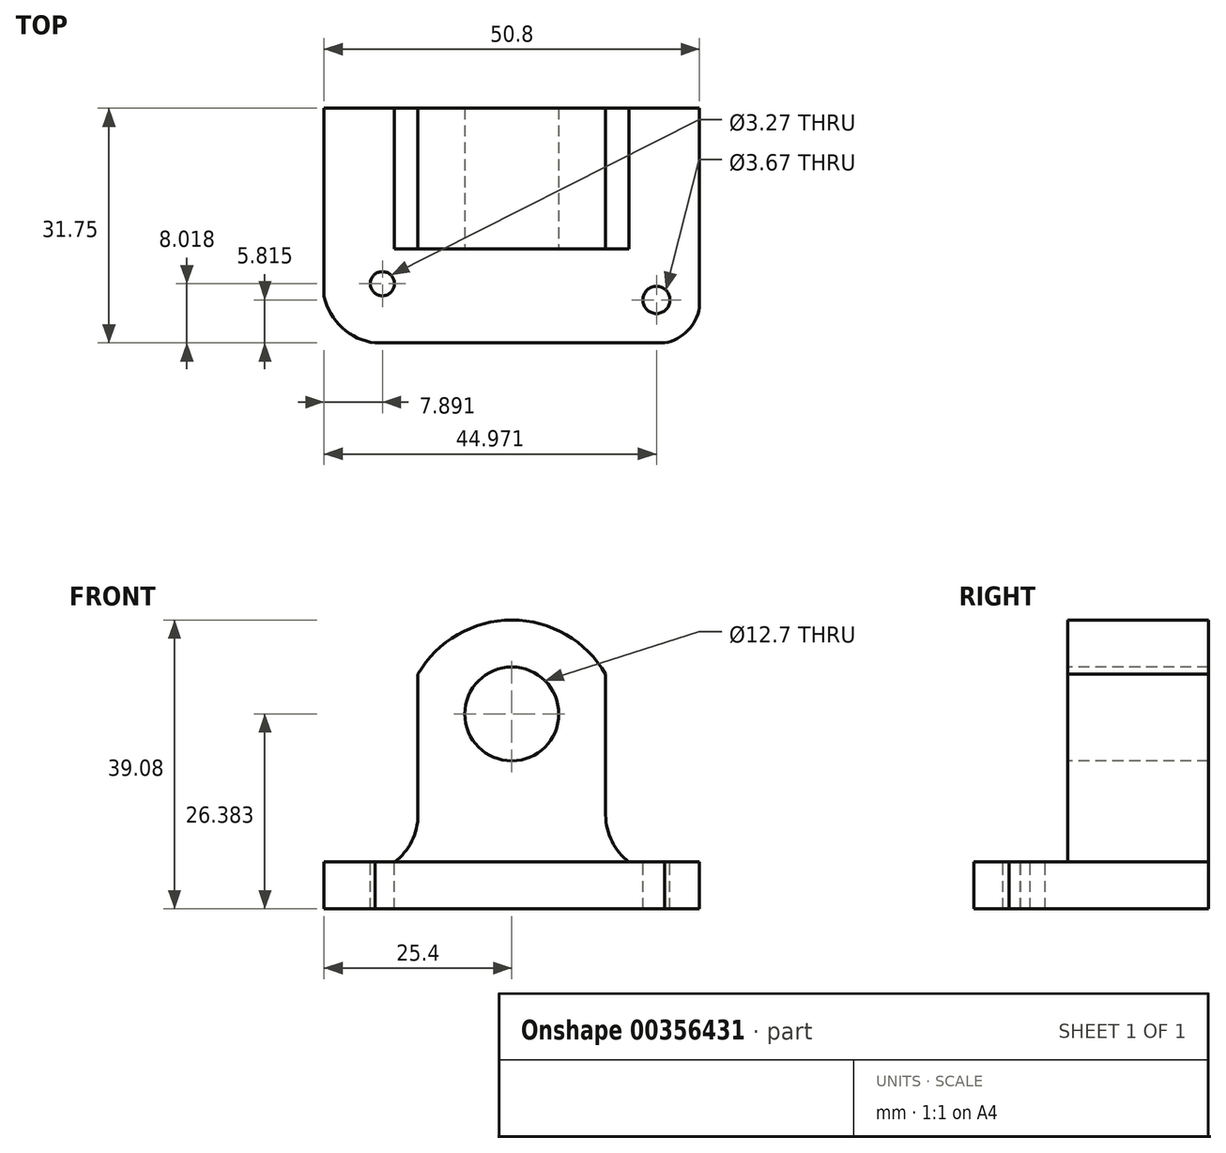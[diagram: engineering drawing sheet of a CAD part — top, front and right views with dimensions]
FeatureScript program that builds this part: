
annotation { "Feature Type Name" : "Feature", "Feature Type Description" : "" }
export const myFeature = defineFeature(function(context is Context, id is Id, definition is map)
    precondition{}
    {
        {
            var Q0;
            Q0=qCreatedBy(makeId("Front.planeOp"),FACE);
            var sketch = newSketch(context, id + "F0", { "sketchPlane" : qUnion([Q0])});
            skLineSegment(sketch, "E0", {"start": v(0, 44.45) * mm, "end": v(0, 0) * mm});
            skLineSegment(sketch, "E1", {"start": v(0, 0) * mm, "end": v(50.8, 0) * mm});
            skLineSegment(sketch, "E2", {"start": v(50.8, 0) * mm, "end": v(50.8, 44.45) * mm});
            skLineSegment(sketch, "E3", {"start": v(50.8, 44.45) * mm, "end": v(0, 44.45) * mm});
            skSolve(sketch);
        }
        {
            var Q0;
            Q0 = qSketchRegion(id + "F0", true);
            extrude(context, id + "F1", {"entities" : qUnion([Q0]), "depth" : 31.75 * mm});
        }
        {
            var Q0;
            Q0=makeQuery(id+"F1.opExtrude","SWEPT_FACE",FACE,{"disambiguationData":[OSD([sQuery(id+"F0.wireOp",EDGE,"E3")])]});
            var sketch = newSketch(context, id + "F2", { "sketchPlane" : qUnion([Q0])});
            skLineSegment(sketch, "E4", {"start": v(0, -19.05) * mm, "end": v(50.8, -19.05) * mm});
            skSolve(sketch);
        }
        {
            var Q0;
            {var subQ0=sQuery(id+"F2.wireOp",EDGE,"E4");Q0=makeQuery(id+"F2.imprint","IMPRINT",FACE,{"disambiguationData":[TD([[makeQuery(id+"F2.imprint","IMPRINT",EDGE,{"derivedFrom":subQ0}),-1.0]])]});}
            extrude(context, id + "F3", {"entities" : qUnion([Q0]), "operationType" : NewBodyOperationType.REMOVE, "oppositeDirection" : true, "depth" : 38.1 * mm});
        }
        {
            var Q0;
            Q0=makeQuery(id+"F3.boolean.opBoolean","COPY",FACE,{"derivedFrom":makeQuery(id+"F3.opExtrude","SWEPT_FACE",FACE,{"disambiguationData":[OSD([sQuery(id+"F2.wireOp",EDGE,"E4")])]})});
            var sketch = newSketch(context, id + "F4", { "sketchPlane" : qUnion([Q0])});
            skLineSegment(sketch, "E5", {"start": v(38.1, 44.45) * mm, "end": v(38.1, 12.7) * mm});
            skArc(sketch, "E6", {"start": v(38.1, 12.7) * mm, "mid": v(42.49, 5.6) * mm, "end": v(50.8, 6.35) * mm});
            skLineSegment(sketch, "E7", {"start": v(12.7, 44.45) * mm, "end": v(12.7, 12.7) * mm});
            skArc(sketch, "E8", {"start": v(0, 6.35) * mm, "mid": v(8.31, 5.6) * mm, "end": v(12.7, 12.7) * mm});
            skSolve(sketch);
        }
        {
            var Q0;
            Q0 = qSketchRegion(id + "F4", true);
            var Q1;
            {var subQ3=sQuery(id+"F4.wireOp",EDGE,"E7");Q1=makeQuery(id+"F4.imprint","IMPRINT",FACE,{"disambiguationData":[TD([[makeQuery(id+"F4.imprint","IMPRINT",EDGE,{"derivedFrom":subQ3}),-1.0]])]});}
            var Q2;
            {var subQ3=sQuery(id+"F4.wireOp",EDGE,"E5");Q2=makeQuery(id+"F4.imprint","IMPRINT",FACE,{"disambiguationData":[TD([[makeQuery(id+"F4.imprint","IMPRINT",EDGE,{"derivedFrom":subQ3}),1.0]])]});}
            extrude(context, id + "F5", {"entities" : qUnion([Q0, Q1, Q2]), "operationType" : NewBodyOperationType.REMOVE, "oppositeDirection" : true, "depth" : 25.4 * mm});
        }
        {
            var Q0;
            Q0=makeQuery(id+"F3.boolean.opBoolean","COPY",FACE,{"derivedFrom":makeQuery(id+"F3.opExtrude","SWEPT_FACE",FACE,{"disambiguationData":[OSD([sQuery(id+"F2.wireOp",EDGE,"E4")])]})});
            var sketch = newSketch(context, id + "F6", { "sketchPlane" : qUnion([Q0])});
            skArc(sketch, "E9", {"start": v(38.1, 31.75) * mm, "mid": v(25.4, 39.08) * mm, "end": v(12.7, 31.75) * mm});
            skSolve(sketch);
        }
        {
            var Q0;
            Q0 = qSketchRegion(id + "F6", true);
            var Q1;
            {var subQ0=sQuery(id+"F6.wireOp",EDGE,"E9");Q1=makeQuery(id+"F6.imprint","IMPRINT",FACE,{"disambiguationData":[TD([[makeQuery(id+"F6.imprint","IMPRINT",EDGE,{"derivedFrom":subQ0}),-1.0]])]});}
            extrude(context, id + "F7", {"entities" : qUnion([Q0, Q1]), "operationType" : NewBodyOperationType.REMOVE, "oppositeDirection" : true, "depth" : 25.4 * mm});
        }
        {
            var Q0;
            Q0=makeQuery(id+"F3.boolean.opBoolean","COPY",FACE,{"derivedFrom":makeQuery(id+"F3.opExtrude","SWEPT_FACE",FACE,{"disambiguationData":[OSD([sQuery(id+"F2.wireOp",EDGE,"E4")])]})});
            var sketch = newSketch(context, id + "F8", { "sketchPlane" : qUnion([Q0])});
            skCircle(sketch, "E10", {"center": v(25.4, 26.38) * mm, "radius": 6.35 * mm});
            skSolve(sketch);
        }
        {
            var Q0;
            Q0=makeQuery(id+"F8.imprint","IMPRINT",FACE,{"disambiguationData":[TD([[makeQuery(id+"F8.imprint","IMPRINT",EDGE,{"derivedFrom":sQuery(id+"F8.wireOp",EDGE,"E10")}),1.0]])]});
            extrude(context, id + "F9", {"entities" : qUnion([Q0]), "operationType" : NewBodyOperationType.REMOVE, "oppositeDirection" : true, "depth" : 25.4 * mm});
        }
        {
            var Q0;
            {var subQ0=sQuery(id+"F4.wireOp",EDGE,"E6");var subQ1=sQuery(id+"F2.wireOp",EDGE,"E4");var subQ2=makeQuery(id+"F3.boolean.opBoolean","COPY",EDGE,{"derivedFrom":makeQuery(id+"F3.opExtrude","CAP_EDGE",EDGE,{"disambiguationData":[OSD([subQ1])],"isStart":false})});var subQ3=sQuery(id+"F0.wireOp",EDGE,"E3");var subQ4=sQuery(id+"F0.wireOp",EDGE,"E2");var subQ5=sQuery(id+"F4.wireOp",EDGE,"E8");var subQ6=sQuery(id+"F0.wireOp",EDGE,"E0");Q0=makeQuery(id+"F5.boolean.opBoolean","MERGE",FACE,{"derivedFrom":[makeQuery(id+"F3.boolean.opBoolean","COPY",FACE,{"derivedFrom":makeQuery(id+"F3.opExtrude","CAP_FACE",FACE,{"disambiguationData":[OSD([subQ6,subQ4,subQ3,subQ1])],"isStart":false})}),makeQuery(id+"F5.opExtrude","SWEPT_FACE",FACE,{"disambiguationData":[OSD([subQ1]),TDD([makeQuery(id+"F4.imprint","IMPRINT",EDGE,{"disambiguationData":[TD([[makeQuery(id+"F4.imprint","INTERSECT",VERTEX,{"derivedFrom":[subQ2,subQ5]}),1.0]])],"derivedFrom":subQ2})])]}),makeQuery(id+"F5.opExtrude","SWEPT_FACE",FACE,{"disambiguationData":[OSD([subQ1]),TDD([makeQuery(id+"F4.imprint","IMPRINT",EDGE,{"disambiguationData":[TD([[makeQuery(id+"F4.imprint","INTERSECT",VERTEX,{"derivedFrom":[subQ2,subQ0]}),-1.0]])],"derivedFrom":subQ2})])]})]});}
            var sketch = newSketch(context, id + "F10", { "sketchPlane" : qUnion([Q0])});
            skArc(sketch, "E11", {"start": v(0, -25.45) * mm, "mid": v(2.45, -29.7) * mm, "end": v(6.92, -31.75) * mm});
            skArc(sketch, "E12", {"start": v(46.1, -31.75) * mm, "mid": v(49.86, -29.28) * mm, "end": v(50.8, -24.88) * mm});
            skSolve(sketch);
        }
        {
            var Q0;
            {var subQ0=sQuery(id+"F10.wireOp",EDGE,"E11");Q0=makeQuery(id+"F10.imprint","IMPRINT",FACE,{"disambiguationData":[TD([[makeQuery(id+"F10.imprint","IMPRINT",EDGE,{"derivedFrom":subQ0}),-1.0]])]});}
            var Q1;
            {var subQ0=sQuery(id+"F10.wireOp",EDGE,"E12");var subQ1=sQuery(id+"F0.wireOp",EDGE,"E3");var subQ2=makeQuery(id+"F3.boolean.opBoolean","COPY",EDGE,{"derivedFrom":makeQuery(id+"F3.opExtrude","CAP_EDGE",EDGE,{"disambiguationData":[OSD([subQ1])],"isStart":false})});var subQ3=makeQuery(id+"F10.imprint","INTERSECT",VERTEX,{"derivedFrom":[subQ2,subQ0]});Q1=makeQuery(id+"F10.imprint","IMPRINT",FACE,{"disambiguationData":[TD([[makeQuery(id+"F10.imprint","IMPRINT",EDGE,{"disambiguationData":[TD([[subQ3,-1.0]])],"derivedFrom":subQ0}),-1.0]])]});}
            extrude(context, id + "F11", {"entities" : qUnion([Q0, Q1]), "operationType" : NewBodyOperationType.REMOVE, "oppositeDirection" : true, "depth" : 25.4 * mm});
        }
        {
            var Q0;
            {var subQ0=sQuery(id+"F4.wireOp",EDGE,"E6");var subQ1=sQuery(id+"F2.wireOp",EDGE,"E4");var subQ2=makeQuery(id+"F3.boolean.opBoolean","COPY",EDGE,{"derivedFrom":makeQuery(id+"F3.opExtrude","CAP_EDGE",EDGE,{"disambiguationData":[OSD([subQ1])],"isStart":false})});var subQ3=sQuery(id+"F0.wireOp",EDGE,"E3");var subQ4=sQuery(id+"F0.wireOp",EDGE,"E2");var subQ5=sQuery(id+"F4.wireOp",EDGE,"E8");var subQ6=sQuery(id+"F0.wireOp",EDGE,"E0");Q0=makeQuery(id+"F5.boolean.opBoolean","MERGE",FACE,{"derivedFrom":[makeQuery(id+"F3.boolean.opBoolean","COPY",FACE,{"derivedFrom":makeQuery(id+"F3.opExtrude","CAP_FACE",FACE,{"disambiguationData":[OSD([subQ6,subQ4,subQ3,subQ1])],"isStart":false})}),makeQuery(id+"F5.opExtrude","SWEPT_FACE",FACE,{"disambiguationData":[OSD([subQ1]),TDD([makeQuery(id+"F4.imprint","IMPRINT",EDGE,{"disambiguationData":[TD([[makeQuery(id+"F4.imprint","INTERSECT",VERTEX,{"derivedFrom":[subQ2,subQ5]}),1.0]])],"derivedFrom":subQ2})])]}),makeQuery(id+"F5.opExtrude","SWEPT_FACE",FACE,{"disambiguationData":[OSD([subQ1]),TDD([makeQuery(id+"F4.imprint","IMPRINT",EDGE,{"disambiguationData":[TD([[makeQuery(id+"F4.imprint","INTERSECT",VERTEX,{"derivedFrom":[subQ2,subQ0]}),-1.0]])],"derivedFrom":subQ2})])]})]});}
            var sketch = newSketch(context, id + "F12", { "sketchPlane" : qUnion([Q0])});
            skCircle(sketch, "E13", {"center": v(7.9, -23.73) * mm, "radius": 1.63 * mm});
            skCircle(sketch, "E14", {"center": v(44.97, -25.94) * mm, "radius": 1.84 * mm});
            skSolve(sketch);
        }
        {
            var Q0;
            Q0=makeQuery(id+"F12.imprint","IMPRINT",FACE,{"disambiguationData":[TD([[makeQuery(id+"F12.imprint","IMPRINT",EDGE,{"derivedFrom":sQuery(id+"F12.wireOp",EDGE,"E14")}),1.0]])]});
            var Q1;
            Q1=makeQuery(id+"F12.imprint","IMPRINT",FACE,{"disambiguationData":[TD([[makeQuery(id+"F12.imprint","IMPRINT",EDGE,{"derivedFrom":sQuery(id+"F12.wireOp",EDGE,"E13")}),1.0]])]});
            extrude(context, id + "F13", {"entities" : qUnion([Q0, Q1]), "operationType" : NewBodyOperationType.REMOVE, "oppositeDirection" : true, "depth" : 25.4 * mm});
        }
    });
